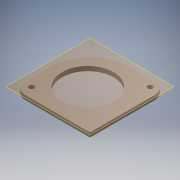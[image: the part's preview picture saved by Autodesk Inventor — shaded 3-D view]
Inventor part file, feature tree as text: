
AUTODESK INVENTOR PART (.ipt)
format: ipt  version: 2016 (Build 200138000, 138)  size: 943,104 bytes
history: native  units: mm
features: extrude x3, sketch x3, reference x2, projected_geometry x2, plane x1
ambient origin geometry x8: Origin, YZ Plane, XZ Plane, XY Plane, X Axis, Y Axis, Z Axis, Center Point
bodies: Solid1 (feature_tree)
feature tree (11):
  plane  "Work Plane1"
  extrude  "Extrusion1"  Depth=3.0mm TaperAngle=0.0deg
  extrude  "Extrusion2"  [1 undecoded]
  extrude  "Extrusion3"  [1 undecoded]
  sketch  "Sketch1"  dims[d0=3.0mm d1=0.0mm d2=1.0mm d3=0.0mm]
  reference  "Reference1"
  reference  "Reference2"
  sketch  "Sketch2"  dims[d4=1.0mm d5=0.0mm]
  projected_geometry  "Projected Loop1"
  sketch  "Sketch3"
  projected_geometry  "Projected Loop2"
note: 2 required parameter values undecoded (feature->parameter linkage not recoverable at this tier; creation-order binding heuristic only, values carry confidence <= 0.55)
